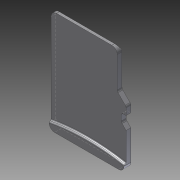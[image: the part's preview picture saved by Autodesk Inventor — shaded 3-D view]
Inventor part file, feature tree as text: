
AUTODESK INVENTOR PART (.ipt)
format: ipt  version: 2011 (Build 150239000, 239)  size: 148,480 bytes
history: native  units: in
note: dims shown in document units (in); Inventor stores cm internally (conversion verified against a paired STEP export)
features: fillet x4, extrude x3, sketch x3
ambient origin geometry x8: Origin, YZ Plane, XZ Plane, XY Plane, X Axis, Y Axis, Z Axis, Center Point
bodies: Solid1 (feature_tree)
feature tree (10):
  extrude  "Extrusion1"  Depth=0.5906in
  fillet  "Fillet1"  Radius=0.9276in
  fillet  "Fillet2"  Radius=0.3819in
  fillet  "Fillet3"  Radius=0.0472in
  extrude  "Extrusion2"  Depth=0.0315in
  extrude  "Extrusion3"  TaperAngle=0.0deg  [1 undecoded]
  fillet  "Fillet4"  Radius=0.0276in
  sketch  "Sketch1"  dims[d0=0.4331in d1=0.5906in d2=0.9276in d5=0.3819in d6=0.0472in]
  sketch  "Sketch3"  dims[d7=0.0276in d8=0.0315in]
  sketch  "Sketch4"  dims[d9=0.311in d11=0.0in d12=0.0276in d13=0.0in d14=0.0315in d15=0.0157in d16=0.0079in d17=0.0205in d18=0.0in d19=0.0118in d20=0.0276in d21=0.0in d22=1.1811in d23=0.0591in d24=0.039in d25=0.039in d26=0.0118in d27=0.0in d28=0.0079in]
note: 1 required parameter value undecoded (feature->parameter linkage not recoverable at this tier; creation-order binding heuristic only, values carry confidence <= 0.55)
